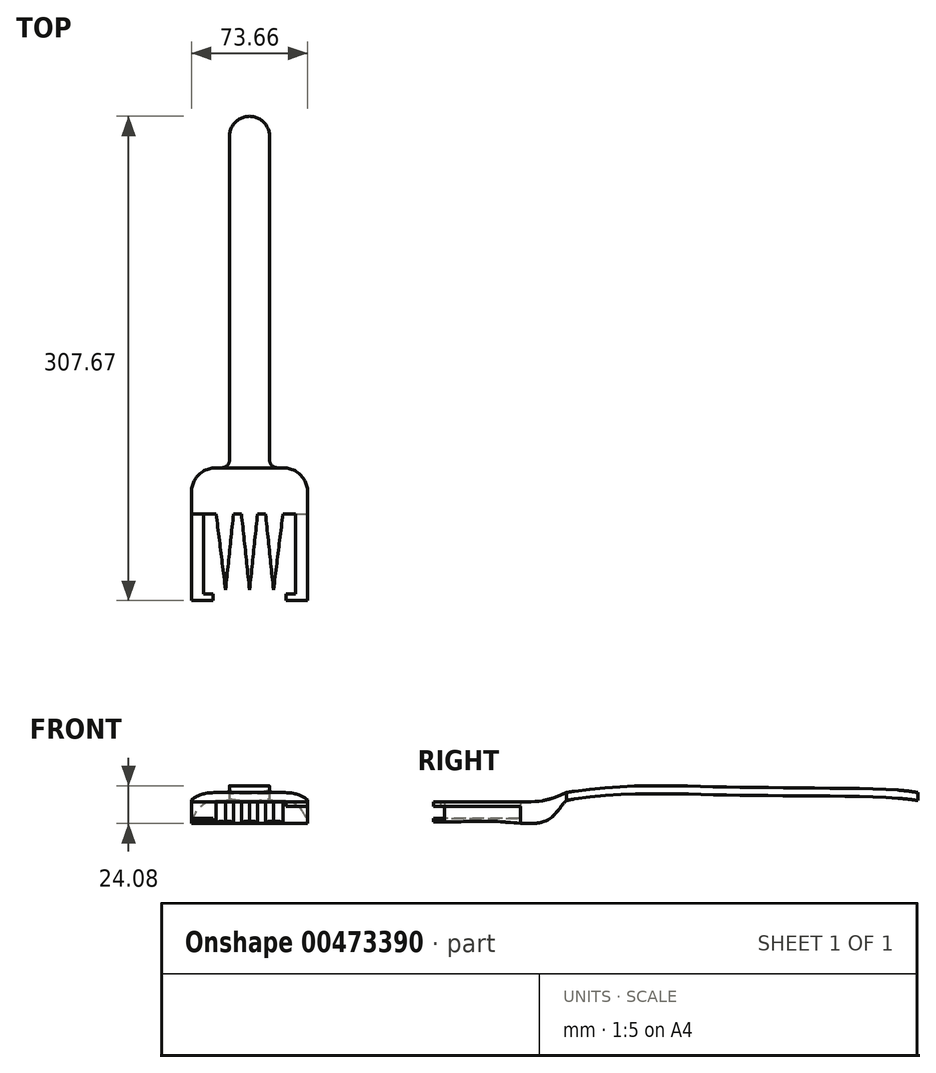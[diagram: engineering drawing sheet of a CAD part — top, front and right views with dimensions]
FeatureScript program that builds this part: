
annotation { "Feature Type Name" : "Feature", "Feature Type Description" : "" }
export const myFeature = defineFeature(function(context is Context, id is Id, definition is map)
    precondition{}
    {
        {
            var Q0;
            Q0=qCreatedBy(makeId("Top.planeOp"),FACE);
            var sketch = newSketch(context, id + "F0", { "sketchPlane" : qUnion([Q0])});
            skLineSegment(sketch, "E0", {"start": v(42, 63.5) * mm, "end": v(42, 0) * mm, "construction": true});
            skPoint(sketch, "E1", {"position": v(26.74, 8.89) * mm});
            skPoint(sketch, "E2", {"position": v(42, 8.89) * mm});
            skLineSegment(sketch, "E3", {"start": v(26.74, 8.89) * mm, "end": v(20.78, 57.15) * mm});
            skLineSegment(sketch, "E4", {"start": v(26.74, 8.89) * mm, "end": v(31.81, 57.15) * mm});
            skLineSegment(sketch, "E5", {"start": v(12.9, 57.15) * mm, "end": v(20.78, 57.15) * mm});
            skLineSegment(sketch, "E6", {"start": v(31.81, 57.15) * mm, "end": v(36.86, 57.15) * mm});
            skLineSegment(sketch, "E7", {"start": v(36.86, 57.15) * mm, "end": v(42, 8.89) * mm});
            skLineSegment(sketch, "E8.MirrorCS", {"start": v(47.13, 57.15) * mm, "end": v(42, 8.89) * mm});
            skPoint(sketch, "E9.MirrorP", {"position": v(57.24, 8.89) * mm});
            skLineSegment(sketch, "E10.MirrorCS", {"start": v(52.18, 57.15) * mm, "end": v(47.13, 57.15) * mm});
            skLineSegment(sketch, "E11.MirrorCS", {"start": v(71.1, 57.15) * mm, "end": v(63.2, 57.15) * mm});
            skLineSegment(sketch, "E12.MirrorCS", {"start": v(57.24, 8.89) * mm, "end": v(52.18, 57.15) * mm});
            skLineSegment(sketch, "E13.MirrorCS", {"start": v(57.24, 8.89) * mm, "end": v(63.2, 57.15) * mm});
            skLineSegment(sketch, "E14", {"start": v(12.9, 57.15) * mm, "end": v(12.9, 6.35) * mm});
            skLineSegment(sketch, "E15", {"start": v(12.9, 6.35) * mm, "end": v(18.85, 6.35) * mm});
            skLineSegment(sketch, "E16", {"start": v(18.85, 6.35) * mm, "end": v(18.85, 1.96) * mm});
            skLineSegment(sketch, "E17", {"start": v(18.85, 1.96) * mm, "end": v(5.16, 1.96) * mm});
            skLineSegment(sketch, "E18", {"start": v(5.16, 1.96) * mm, "end": v(5.16, 57.15) * mm});
            skLineSegment(sketch, "E19.MirrorCS", {"start": v(65.14, 6.35) * mm, "end": v(65.14, 1.96) * mm});
            skLineSegment(sketch, "E20.MirrorCS", {"start": v(71.1, 6.35) * mm, "end": v(65.14, 6.35) * mm});
            skLineSegment(sketch, "E21.MirrorCS", {"start": v(65.14, 1.96) * mm, "end": v(78.82, 1.96) * mm});
            skLineSegment(sketch, "E22.MirrorCS", {"start": v(71.1, 57.15) * mm, "end": v(71.1, 6.35) * mm});
            skLineSegment(sketch, "E23.MirrorCS", {"start": v(78.82, 1.96) * mm, "end": v(78.82, 57.15) * mm});
            skLineSegment(sketch, "E24", {"start": v(5.16, 57.15) * mm, "end": v(5.16, 63.5) * mm});
            skLineSegment(sketch, "E25", {"start": v(78.82, 57.15) * mm, "end": v(78.82, 63.5) * mm});
            skPoint(sketch, "E26.left.start.orphan", {"position": v(0, 0) * mm});
            skPoint(sketch, "E27.orphan", {"position": v(84.1, 63.5) * mm});
            skLineSegment(sketch, "E28.top", {"start": v(5.16, 86.36) * mm, "end": v(29.3, 86.36) * mm});
            skLineSegment(sketch, "E28.left", {"start": v(5.16, 63.5) * mm, "end": v(5.16, 86.36) * mm});
            skLineSegment(sketch, "E28.right", {"start": v(78.82, 63.5) * mm, "end": v(78.82, 86.36) * mm});
            skLineSegment(sketch, "E29.top", {"start": v(29.3, 309.63) * mm, "end": v(54.7, 309.63) * mm});
            skLineSegment(sketch, "E29.left", {"start": v(29.3, 86.36) * mm, "end": v(29.3, 309.63) * mm});
            skLineSegment(sketch, "E29.right", {"start": v(54.7, 86.36) * mm, "end": v(54.7, 309.63) * mm});
            skLineSegment(sketch, "E30.trimOffspring", {"start": v(54.7, 86.36) * mm, "end": v(78.82, 86.36) * mm});
            skSolve(sketch);
        }
        {
            var Q0;
            Q0=makeQuery(id+"F0.imprint","IMPRINT",FACE,{"disambiguationData":[TD([[makeQuery(id+"F0.imprint","IMPRINT",EDGE,{"derivedFrom":sQuery(id+"F0.wireOp",EDGE,"E3")}),-1.0]])]});
            extrude(context, id + "F1", {"entities" : qUnion([Q0]), "depth" : 101.6 * mm});
        }
        {
            var Q0;
            Q0=makeQuery(id+"F1.opExtrude","SWEPT_FACE",FACE,{"disambiguationData":[OSD([sQuery(id+"F0.wireOp",EDGE,"E29.right")])]});
            var sketch = newSketch(context, id + "F2", { "sketchPlane" : qUnion([Q0])});
            skLineSegment(sketch, "E31.0", {"start": v(86.36, 101.6) * mm, "end": v(86.36, 50.8) * mm});
            skLineSegment(sketch, "E31.1", {"start": v(86.36, 101.6) * mm, "end": v(309.63, 101.6) * mm});
            skLineSegment(sketch, "E31.2", {"start": v(309.63, 101.6) * mm, "end": v(309.63, 50.8) * mm});
            skLineSegment(sketch, "E31.3", {"start": v(86.36, 0) * mm, "end": v(309.63, 0) * mm});
            skFitSpline(sketch, "E32", {"points": [v(309.63, 50.8) * mm, v(274.25, 53.34) * mm, v(221.31, 53.85) * mm, v(176.46, 54.61) * mm, v(137.88, 55.12) * mm, v(86.36, 50.8) * mm], "startDerivative": vector(-185.69, 32.31) * mm, "endDerivative": vector(-247.75, -43.39) * mm});
            skFitSpline(sketch, "E33", {"points": [v(309.63, 45.72) * mm, v(274.25, 48.26) * mm, v(220.87, 48.77) * mm, v(176.9, 49.53) * mm, v(139.22, 50.04) * mm, v(86.36, 45.72) * mm], "startDerivative": vector(-185.5, 29.48) * mm, "endDerivative": vector(-251.8, -52.09) * mm});
            skLineSegment(sketch, "E34.trimOffspring", {"start": v(86.36, 45.72) * mm, "end": v(86.36, 0) * mm});
            skLineSegment(sketch, "E35.trimOffspring", {"start": v(309.63, 45.72) * mm, "end": v(309.63, 0) * mm});
            skSolve(sketch);
        }
        {
            var Q0;
            Q0=makeQuery(id+"F2.imprint","IMPRINT",FACE,{"disambiguationData":[TD([[makeQuery(id+"F2.imprint","IMPRINT",EDGE,{"derivedFrom":sQuery(id+"F2.wireOp",EDGE,"E31.3")}),1.0]])]});
            var Q1;
            Q1=makeQuery(id+"F2.imprint","IMPRINT",FACE,{"disambiguationData":[TD([[makeQuery(id+"F2.imprint","IMPRINT",EDGE,{"derivedFrom":sQuery(id+"F2.wireOp",EDGE,"E31.0")}),1.0]])]});
            extrude(context, id + "F3", {"entities" : qUnion([Q0, Q1]), "operationType" : NewBodyOperationType.REMOVE, "oppositeDirection" : true, "depth" : 25.4 * mm});
        }
        {
            var Q0;
            Q0=makeQuery(id+"F1.opExtrude","SWEPT_FACE",FACE,{"disambiguationData":[OSD([sQuery(id+"F0.wireOp",EDGE,"E23.MirrorCS"),sQuery(id+"F0.wireOp",EDGE,"E25"),sQuery(id+"F0.wireOp",EDGE,"E28.right")])]});
            var sketch = newSketch(context, id + "F4", { "sketchPlane" : qUnion([Q0])});
            skLineSegment(sketch, "E36.0", {"start": v(86.36, 101.6) * mm, "end": v(86.36, 50.8) * mm});
            skPoint(sketch, "E37.0", {"position": v(44.16, 101.6) * mm});
            skLineSegment(sketch, "E38.0", {"start": v(1.96, 101.6) * mm, "end": v(86.36, 101.6) * mm});
            skLineSegment(sketch, "E39.0", {"start": v(1.96, 101.6) * mm, "end": v(1.96, 44.74) * mm});
            skLineSegment(sketch, "E40.0", {"start": v(1.96, 0) * mm, "end": v(86.36, 0) * mm});
            skFitSpline(sketch, "E41.0", {"points": [v(309.63, 50.8) * mm, v(298.57, 52.72) * mm, v(273.86, 53.58) * mm, v(221.2, 53.72) * mm, v(176.6, 54.51) * mm, v(137.55, 55.75) * mm, v(104.18, 53.92) * mm, v(86.36, 50.8) * mm]});
            skFitSpline(sketch, "E42.0", {"points": [v(309.63, 45.72) * mm, v(298.57, 47.48) * mm, v(273.9, 48.6) * mm, v(220.8, 48.59) * mm, v(177.03, 49.51) * mm, v(138.84, 50.4) * mm, v(104.7, 49.52) * mm, v(86.36, 45.72) * mm]});
            skFitSpline(sketch, "E43", {"points": [v(86.36, 45.72) * mm, v(74.43, 33.37) * mm, v(44.15, 32.24) * mm, v(1.96, 32.04) * mm], "startDerivative": vector(-42.52, -37.37) * mm, "endDerivative": vector(-105.76, 0.67) * mm});
            skFitSpline(sketch, "E44", {"points": [v(86.36, 50.8) * mm, v(71.49, 45.72) * mm, v(43.42, 44.94) * mm, v(1.96, 44.74) * mm], "startDerivative": vector(-54.11, -21.48) * mm, "endDerivative": vector(-106.87, 0.66) * mm});
            skLineSegment(sketch, "E45.trimOffspring", {"start": v(1.96, 32.04) * mm, "end": v(1.96, 0) * mm});
            skLineSegment(sketch, "E46.trimOffspring", {"start": v(86.36, 45.72) * mm, "end": v(86.36, 0) * mm});
            skSolve(sketch);
        }
        {
            var Q0;
            Q0 = qSketchRegion(id + "F4", true);
            extrude(context, id + "F5", {"entities" : qUnion([Q0]), "operationType" : NewBodyOperationType.REMOVE, "endBound" : BoundingType.THROUGH_ALL, "oppositeDirection" : true, "depth" : 25.4 * mm});
        }
        {
            var Q0;
            Q0=qCreatedBy(makeId("Top.planeOp"),FACE);
            var sketch = newSketch(context, id + "F6", { "sketchPlane" : qUnion([Q0])});
            skLineSegment(sketch, "E47.0", {"start": v(54.7, 86.36) * mm, "end": v(78.82, 86.36) * mm});
            skFitSpline(sketch, "E48.0", {"points": [v(78.82, 86.36) * mm, v(78.82, 81.8) * mm, v(78.82, 71.13) * mm, v(78.82, 42.09) * mm, v(78.82, 16.57) * mm, v(78.82, 1.96) * mm]});
            skLineSegment(sketch, "E49.0", {"start": v(65.14, 1.96) * mm, "end": v(78.82, 1.96) * mm});
            skFitSpline(sketch, "E50.0", {"points": [v(5.16, 1.96) * mm, v(5.16, 16.57) * mm, v(5.16, 42.09) * mm, v(5.16, 71.13) * mm, v(5.16, 81.8) * mm, v(5.16, 86.36) * mm]});
            skLineSegment(sketch, "E51.0", {"start": v(5.16, 86.36) * mm, "end": v(12.9, 86.36) * mm});
            skLineSegment(sketch, "E52.0", {"start": v(5.16, 86.36) * mm, "end": v(29.3, 86.36) * mm});
            skFitSpline(sketch, "E53.0", {"points": [v(12.9, 86.36) * mm, v(12.9, 81.8) * mm, v(12.9, 71.13) * mm, v(12.9, 42.09) * mm, v(12.9, 16.57) * mm, v(12.9, 1.96) * mm]});
            skFitSpline(sketch, "E54", {"points": [v(5.16, 68.65) * mm, v(7.16, 73.06) * mm, v(10.75, 78.13) * mm, v(15, 83.52) * mm, v(18.92, 86.36) * mm], "startDerivative": vector(7.41, 19.15) * mm, "endDerivative": vector(17.3, 10.48) * mm});
            skLineSegment(sketch, "E55.0", {"start": v(29.3, 86.36) * mm, "end": v(54.7, 86.36) * mm});
            skLineSegment(sketch, "E56", {"start": v(5.16, 68.65) * mm, "end": v(5.16, 86.36) * mm});
            skSolve(sketch);
        }
        {
            var Q0;
            Q0=qCreatedBy(makeId("Top.planeOp"),FACE);
            cPlane(context, id + "F7", {"entities" : qUnion([Q0]), "cplaneType" : CPlaneType.OFFSET, "offset" : 50.8 * mm, "width" : 152.4 * mm, "height" : 152.4 * mm});
        }
        {
            var Q0;
            Q0=qCreatedBy(id+"F7.planeOp",FACE);
            var sketch = newSketch(context, id + "F8", { "sketchPlane" : qUnion([Q0])});
            skFitSpline(sketch, "E57.0", {"points": [v(5.16, 1.96) * mm, v(5.16, 16.57) * mm, v(5.16, 42.09) * mm, v(5.16, 71.13) * mm, v(5.16, 81.8) * mm, v(5.16, 86.36) * mm]});
            skLineSegment(sketch, "E58.0", {"start": v(5.16, 1.96) * mm, "end": v(18.85, 1.96) * mm});
            skFitSpline(sketch, "E59.0", {"points": [v(18.85, 86.36) * mm, v(18.85, 81.8) * mm, v(18.85, 71.13) * mm, v(18.85, 42.09) * mm, v(18.85, 16.57) * mm, v(18.85, 1.96) * mm]});
            skLineSegment(sketch, "E60.0", {"start": v(12.9, 6.35) * mm, "end": v(18.85, 6.35) * mm});
            skFitSpline(sketch, "E61.0", {"points": [v(12.9, 86.36) * mm, v(12.9, 81.8) * mm, v(12.9, 71.13) * mm, v(12.9, 42.09) * mm, v(12.9, 16.57) * mm, v(12.9, 1.96) * mm]});
            skLineSegment(sketch, "E62", {"start": v(12.9, 57.15) * mm, "end": v(5.16, 57.15) * mm});
            skPoint(sketch, "E63.orphan", {"position": v(5.16, 86.36) * mm});
            skSolve(sketch);
        }
        {
            var Q0;
            Q0 = qSketchRegion(id + "F8", true);
            extrude(context, id + "F9", {"entities" : qUnion([Q0]), "operationType" : NewBodyOperationType.REMOVE, "oppositeDirection" : true, "depth" : 16.5 * mm});
        }
        {
            var Q0;
            Q0=qCreatedBy(makeId("Top.planeOp"),FACE);
            cPlane(context, id + "F10", {"entities" : qUnion([Q0]), "cplaneType" : CPlaneType.OFFSET, "offset" : 30.48 * mm, "width" : 152.4 * mm, "height" : 152.4 * mm});
        }
        {
            var Q0;
            Q0=qCreatedBy(id+"F10.planeOp",FACE);
            var sketch = newSketch(context, id + "F11", { "sketchPlane" : qUnion([Q0])});
            skFitSpline(sketch, "E64.0", {"points": [v(71.1, 86.36) * mm, v(71.1, 81.8) * mm, v(71.1, 71.13) * mm, v(71.1, 42.09) * mm, v(71.1, 16.57) * mm, v(71.1, 1.96) * mm]});
            skLineSegment(sketch, "E65.0", {"start": v(65.14, 1.96) * mm, "end": v(78.82, 1.96) * mm});
            skLineSegment(sketch, "E66.0", {"start": v(71.1, 6.35) * mm, "end": v(65.14, 6.35) * mm});
            skFitSpline(sketch, "E67.0", {"points": [v(65.14, 86.36) * mm, v(65.14, 81.8) * mm, v(65.14, 71.13) * mm, v(65.14, 42.09) * mm, v(65.14, 16.57) * mm, v(65.14, 1.96) * mm]});
            skFitSpline(sketch, "E68.0", {"points": [v(78.82, 86.36) * mm, v(78.82, 81.8) * mm, v(78.82, 71.13) * mm, v(78.82, 42.09) * mm, v(78.82, 16.57) * mm, v(78.82, 1.96) * mm]});
            skLineSegment(sketch, "E69", {"start": v(71.1, 57.15) * mm, "end": v(78.82, 57.15) * mm});
            skPoint(sketch, "E70.orphan", {"position": v(78.82, 86.36) * mm});
            skSolve(sketch);
        }
        {
            var Q0;
            Q0 = qSketchRegion(id + "F11", true);
            extrude(context, id + "F12", {"entities" : qUnion([Q0]), "operationType" : NewBodyOperationType.REMOVE, "depth" : 11.43 * mm});
        }
        {
            var Q0;
            Q0 = qSketchRegion(id + "F6", true);
            extrude(context, id + "F13", {"entities" : qUnion([Q0]), "operationType" : NewBodyOperationType.REMOVE, "oppositeDirection" : true, "depth" : 25.4 * mm});
        }
        {
            var Q0;
            Q0=makeQuery(id+"F1.opExtrude","SWEPT_EDGE",EDGE,{"disambiguationData":[OSD([sQuery(id+"F0.wireOp",EDGE,"E28.right"),sQuery(id+"F0.wireOp",EDGE,"E30.trimOffspring")])]});
            fillet(context, id + "F14", {"entities" : qUnion([Q0]), "radius" : 15.24 * mm, "tangentPropagation" : true, "allowEdgeOverflow" : false});
        }
        {
            var Q0;
            Q0=makeQuery(id+"F1.opExtrude","SWEPT_EDGE",EDGE,{"disambiguationData":[OSD([sQuery(id+"F0.wireOp",EDGE,"E28.top"),sQuery(id+"F0.wireOp",EDGE,"E28.left")])]});
            fillet(context, id + "F15", {"entities" : qUnion([Q0]), "radius" : 15.24 * mm, "tangentPropagation" : true, "allowEdgeOverflow" : false});
        }
        {
            var Q0;
            Q0=makeQuery(id+"F1.opExtrude","SWEPT_EDGE",EDGE,{"disambiguationData":[OSD([sQuery(id+"F0.wireOp",EDGE,"E28.top"),sQuery(id+"F0.wireOp",EDGE,"E29.left")])]});
            fillet(context, id + "F16", {"entities" : qUnion([Q0]), "radius" : 5.08 * mm, "tangentPropagation" : true, "allowEdgeOverflow" : false});
        }
        {
            var Q0;
            Q0=makeQuery(id+"F1.opExtrude","SWEPT_EDGE",EDGE,{"disambiguationData":[OSD([sQuery(id+"F0.wireOp",EDGE,"E29.right"),sQuery(id+"F0.wireOp",EDGE,"E30.trimOffspring")])]});
            fillet(context, id + "F17", {"entities" : qUnion([Q0]), "radius" : 5.08 * mm, "tangentPropagation" : true, "allowEdgeOverflow" : false});
        }
        {
            var Q0;
            Q0=makeQuery(id+"F1.opExtrude","SWEPT_EDGE",EDGE,{"disambiguationData":[OSD([sQuery(id+"F0.wireOp",EDGE,"E29.top"),sQuery(id+"F0.wireOp",EDGE,"E29.right")])]});
            var Q1;
            Q1=makeQuery(id+"F1.opExtrude","SWEPT_EDGE",EDGE,{"disambiguationData":[OSD([sQuery(id+"F0.wireOp",EDGE,"E29.top"),sQuery(id+"F0.wireOp",EDGE,"E29.left")])]});
            fillet(context, id + "F18", {"entities" : qUnion([Q0, Q1]), "radius" : 12.7 * mm, "tangentPropagation" : true, "allowEdgeOverflow" : false});
        }
    });
